AUTODESK INVENTOR PART (.ipt)
format: ipt  version: 2017 SP1 (Build 210196100, 196)  size: 149,504 bytes
history: native  units: in
note: dims shown in document units (in); Inventor stores cm internally (conversion verified against a paired STEP export)
features: extrude x1, fillet x1, sketch x1
ambient origin geometry x8: Origin, YZ Plane, XZ Plane, XY Plane, X Axis, Y Axis, Z Axis, Center Point
bodies: Solid1 (feature_tree)
feature tree (3):
  extrude  "Extrusion1"  Depth=1.1811in
  fillet  "Fillet1"  Radius=1.1417in
  sketch  "Sketch1"  dims[d0=5.748in d1=1.1654in d2=1.1417in d3=0.0in d4=0.315in d5=3.937in d6=2.3622in d7=0.4331in d8=1.1811in d9=2.3622in d11=360.0deg]
